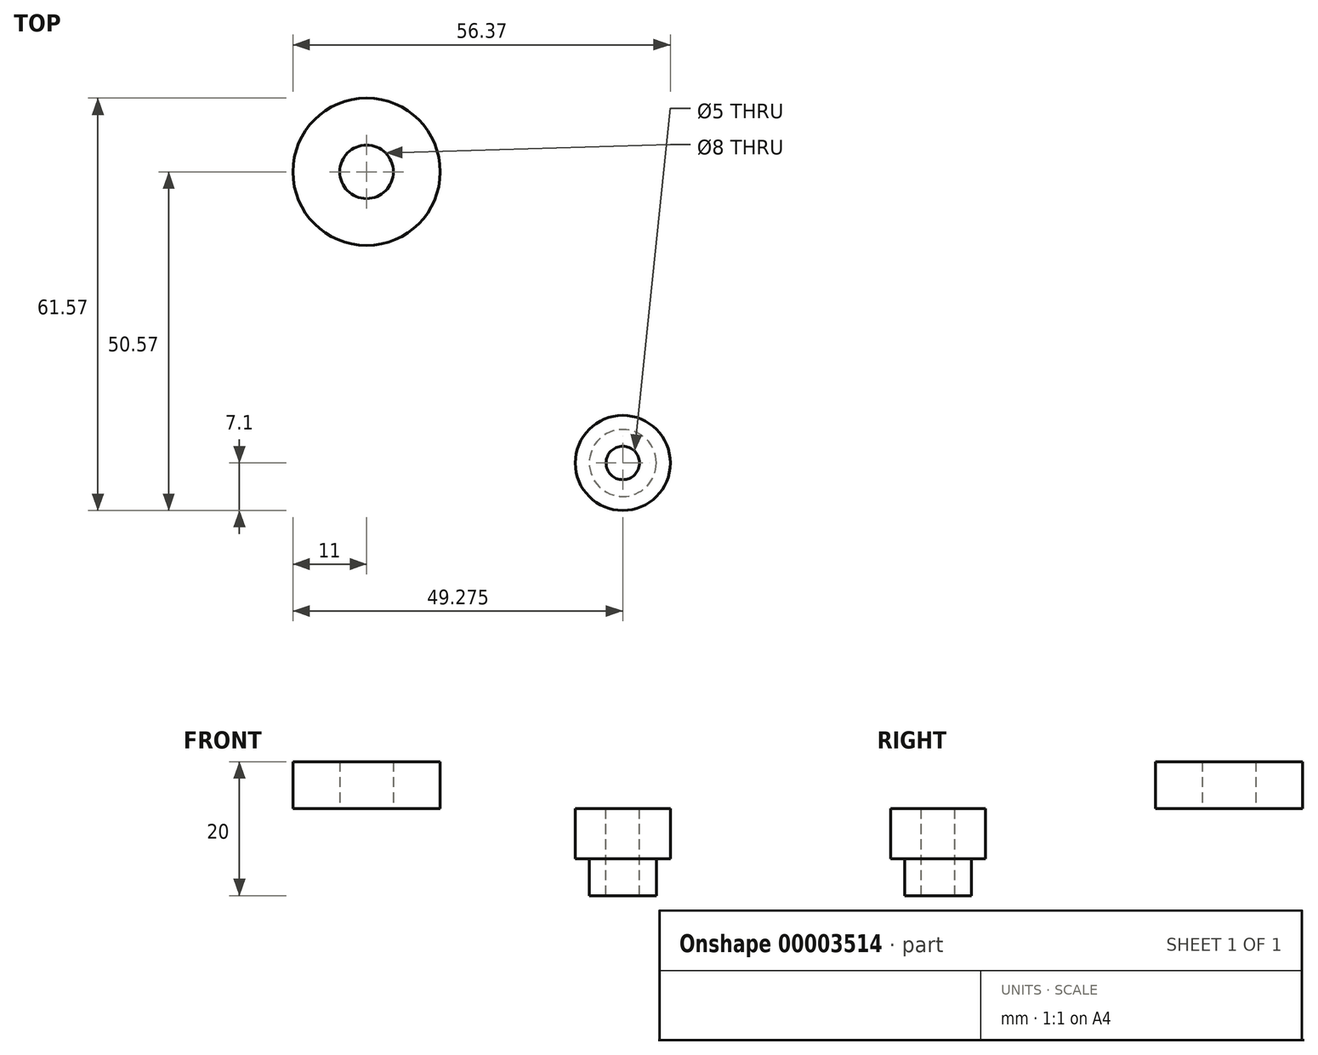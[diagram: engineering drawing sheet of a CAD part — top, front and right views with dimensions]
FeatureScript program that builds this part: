
annotation { "Feature Type Name" : "Feature", "Feature Type Description" : "" }
export const myFeature = defineFeature(function(context is Context, id is Id, definition is map)
    precondition{}
    {
        {
            var Q0;
            Q0=qCreatedBy(makeId("Top.planeOp"),FACE);
            var sketch = newSketch(context, id + "F0", { "sketchPlane" : qUnion([Q0])});
            skCircle(sketch, "E0", {"center": v(0, 0) * mm, "radius": 11 * mm});
            skCircle(sketch, "E1", {"center": v(0, 0) * mm, "radius": 4 * mm});
            skCircle(sketch, "E2", {"center": v(38.27, -43.47) * mm, "radius": 7.1 * mm});
            skCircle(sketch, "E3", {"center": v(38.27, -43.47) * mm, "radius": 2.5 * mm});
            skCircle(sketch, "E4", {"center": v(38.27, -43.47) * mm, "radius": 5 * mm});
            skSolve(sketch);
        }
        {
            var Q0;
            Q0=makeQuery(id+"F0.imprint","IMPRINT",FACE,{"disambiguationData":[TD([[makeQuery(id+"F0.imprint","IMPRINT",EDGE,{"derivedFrom":sQuery(id+"F0.wireOp",EDGE,"E0")}),1.0]])]});
            extrude(context, id + "F1", {"entities" : qUnion([Q0]), "depth" : 7 * mm});
        }
        {
            var Q0;
            Q0=makeQuery(id+"F0.imprint","IMPRINT",FACE,{"disambiguationData":[TD([[makeQuery(id+"F0.imprint","IMPRINT",EDGE,{"derivedFrom":sQuery(id+"F0.wireOp",EDGE,"E3")}),-1.0]])]});
            extrude(context, id + "F2", {"entities" : qUnion([Q0]), "oppositeDirection" : true, "depth" : 13 * mm});
        }
        {
            var Q0;
            Q0=makeQuery(id+"F0.imprint","IMPRINT",FACE,{"disambiguationData":[TD([[makeQuery(id+"F0.imprint","IMPRINT",EDGE,{"derivedFrom":sQuery(id+"F0.wireOp",EDGE,"E2")}),1.0]])]});
            extrude(context, id + "F3", {"entities" : qUnion([Q0]), "operationType" : NewBodyOperationType.ADD, "oppositeDirection" : true, "depth" : 7.5 * mm});
        }
    });
